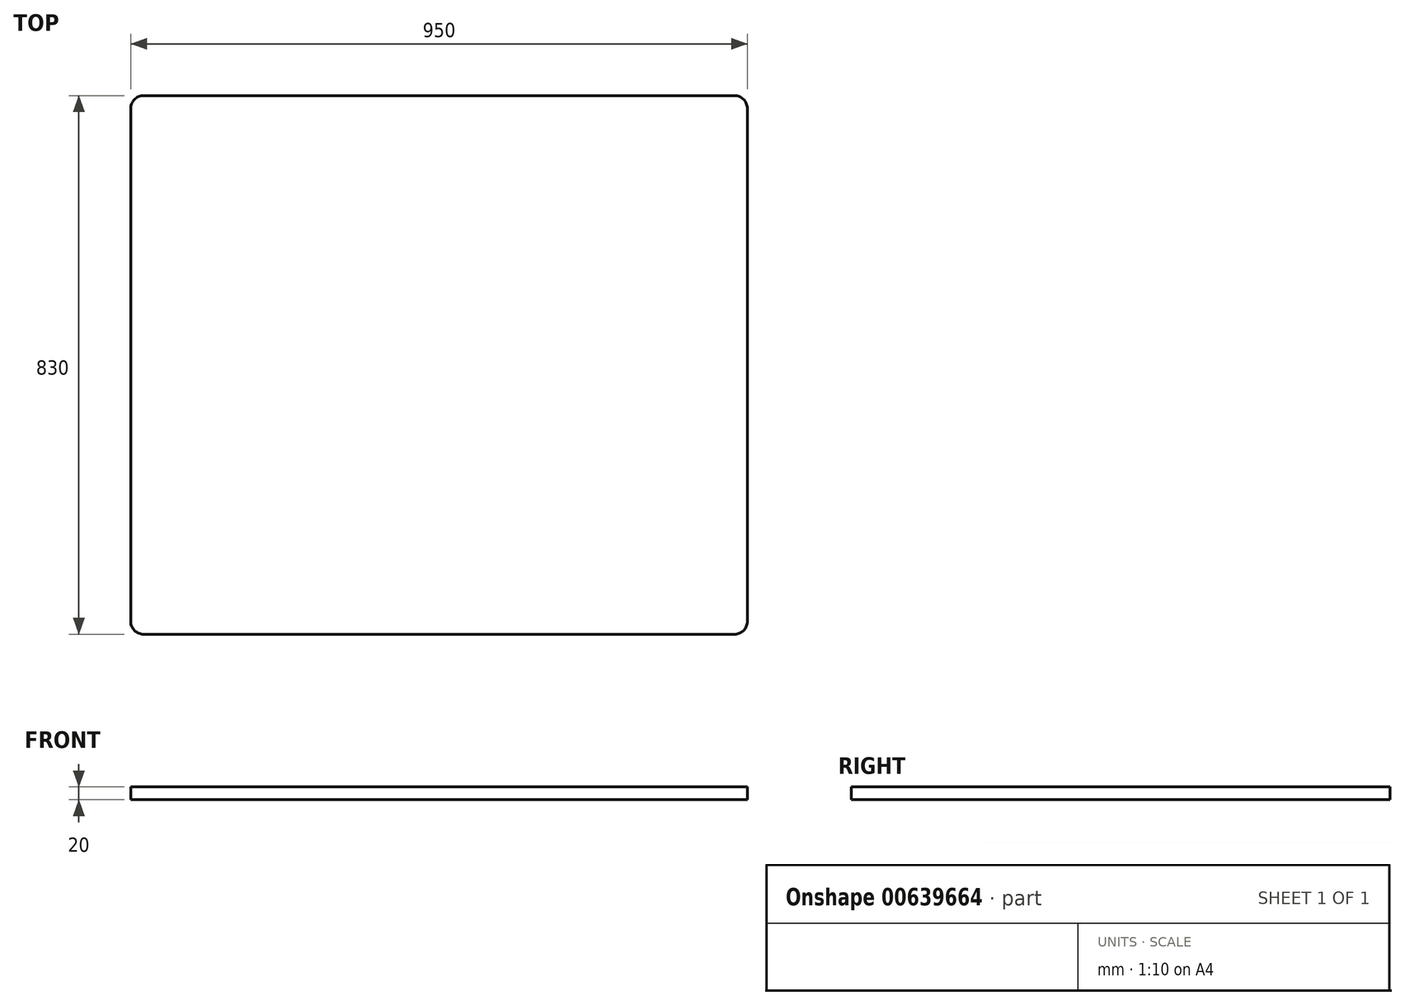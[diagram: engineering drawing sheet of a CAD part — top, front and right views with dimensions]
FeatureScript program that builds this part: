
annotation { "Feature Type Name" : "Feature", "Feature Type Description" : "" }
export const myFeature = defineFeature(function(context is Context, id is Id, definition is map)
    precondition{}
    {
        {
            var Q0;
            Q0=qCreatedBy(makeId("Top.planeOp"),FACE);
            var sketch = newSketch(context, id + "F0", { "sketchPlane" : qUnion([Q0])});
            skLineSegment(sketch, "E0.bottom", {"start": v(20, 0) * mm, "end": v(930, 0) * mm});
            skLineSegment(sketch, "E0.top", {"start": v(20, 830) * mm, "end": v(930, 830) * mm});
            skLineSegment(sketch, "E0.left", {"start": v(0, 20) * mm, "end": v(0, 810) * mm});
            skLineSegment(sketch, "E0.right", {"start": v(950, 20) * mm, "end": v(950, 810) * mm});
            skPoint(sketch, "E1.visualSharp", {"position": v(0, 0) * mm});
            skArc(sketch, "E1.filletArc", {"start": v(0, 20) * mm, "mid": v(5.86, 5.86) * mm, "end": v(20, 0) * mm});
            skPoint(sketch, "E2.visualSharp", {"position": v(0, 830) * mm});
            skArc(sketch, "E2.filletArc", {"start": v(20, 830) * mm, "mid": v(5.86, 824.14) * mm, "end": v(0, 810) * mm});
            skPoint(sketch, "E3.visualSharp", {"position": v(950, 830) * mm});
            skArc(sketch, "E3.filletArc", {"start": v(950, 810) * mm, "mid": v(944.14, 824.14) * mm, "end": v(930, 830) * mm});
            skPoint(sketch, "E4.visualSharp", {"position": v(950, 0) * mm});
            skArc(sketch, "E4.filletArc", {"start": v(930, 0) * mm, "mid": v(944.14, 5.86) * mm, "end": v(950, 20) * mm});
            skSolve(sketch);
        }
        {
            var Q0;
            Q0=makeQuery(id+"F0.imprint","IMPRINT",FACE,{"disambiguationData":[TD([[makeQuery(id+"F0.imprint","IMPRINT",EDGE,{"derivedFrom":sQuery(id+"F0.wireOp",EDGE,"E0.bottom")}),1.0]])]});
            extrude(context, id + "F1", {"entities" : qUnion([Q0]), "depth" : 20 * mm, "offsetDistance" : 25 * mm});
        }
    });
